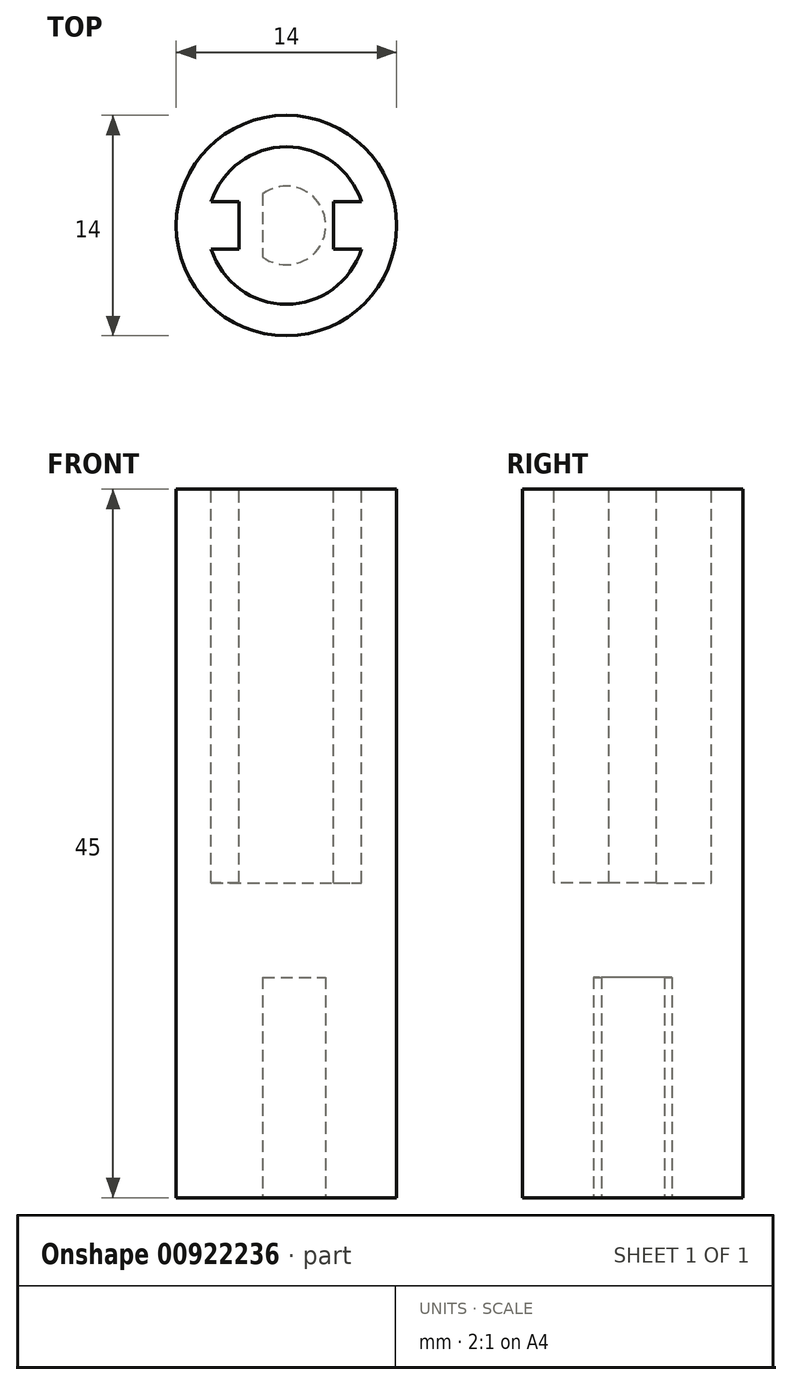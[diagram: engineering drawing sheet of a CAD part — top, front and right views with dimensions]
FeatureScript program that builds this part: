
annotation { "Feature Type Name" : "Feature", "Feature Type Description" : "" }
export const myFeature = defineFeature(function(context is Context, id is Id, definition is map)
    precondition{}
    {
        {
            var Q0;
            Q0=qCreatedBy(makeId("Top.planeOp"),FACE);
            var sketch = newSketch(context, id + "F0", { "sketchPlane" : qUnion([Q0])});
            skCircle(sketch, "E0", {"center": v(0, 0) * mm, "radius": 7 * mm});
            skSolve(sketch);
        }
        {
            var Q0;
            Q0=qSketchRegion(id+"F0",true);
            extrude(context, id + "F1", {"entities" : qUnion([Q0]), "depth" : 45 * mm, "offsetDistance" : 25 * mm});
        }
        {
            var Q0;
            Q0=makeQuery(id+"F1.opExtrude","CAP_FACE",FACE,{"disambiguationData":[OSD([sQuery(id+"F0.wireOp",EDGE,"E0")])],"isStart":false});
            var sketch = newSketch(context, id + "F2", { "sketchPlane" : qUnion([Q0])});
            skLineSegment(sketch, "E1", {"start": v(-12.72, 0) * mm, "end": v(15, 0) * mm, "construction": true});
            skLineSegment(sketch, "E2", {"start": v(0, 9.15) * mm, "end": v(0, -8.81) * mm, "construction": true});
            skLineSegment(sketch, "E3", {"start": v(-4.77, 1.5) * mm, "end": v(-3, 1.5) * mm});
            skLineSegment(sketch, "E4", {"start": v(-3, 1.5) * mm, "end": v(-3, -1.5) * mm});
            skLineSegment(sketch, "E5", {"start": v(-3, -1.5) * mm, "end": v(-4.77, -1.5) * mm});
            skLineSegment(sketch, "E6", {"start": v(4.77, 1.5) * mm, "end": v(3, 1.5) * mm});
            skLineSegment(sketch, "E7", {"start": v(3, 1.5) * mm, "end": v(3, -1.5) * mm});
            skLineSegment(sketch, "E8", {"start": v(3, -1.5) * mm, "end": v(4.77, -1.5) * mm});
            skArc(sketch, "E9", {"start": v(-4.77, -1.5) * mm, "mid": v(0, -5) * mm, "end": v(4.77, -1.5) * mm});
            skArc(sketch, "E10", {"start": v(4.77, 1.5) * mm, "mid": v(0, 5) * mm, "end": v(-4.77, 1.5) * mm});
            skSolve(sketch);
        }
        {
            var Q0;
            Q0=makeQuery(id+"F2.imprint","IMPRINT",FACE,{"disambiguationData":[TD([[makeQuery(id+"F2.imprint","IMPRINT",EDGE,{"derivedFrom":sQuery(id+"F2.wireOp",EDGE,"E3")}),1.0]])]});
            extrude(context, id + "F3", {"entities" : qUnion([Q0]), "operationType" : NewBodyOperationType.REMOVE, "oppositeDirection" : true, "depth" : 25 * mm, "offsetDistance" : 25 * mm});
        }
        {
            var Q0;
            Q0=makeQuery(id+"F1.opExtrude","CAP_FACE",FACE,{"disambiguationData":[OSD([sQuery(id+"F0.wireOp",EDGE,"E0")])],"isStart":true});
            var sketch = newSketch(context, id + "F4", { "sketchPlane" : qUnion([Q0])});
            skCircle(sketch, "E11", {"center": v(0, 0) * mm, "radius": 2.55 * mm});
            skSolve(sketch);
        }
        {
            var Q0;
            Q0=makeQuery(id+"F4.imprint","IMPRINT",FACE,{"disambiguationData":[TD([[makeQuery(id+"F4.imprint","IMPRINT",EDGE,{"derivedFrom":sQuery(id+"F4.wireOp",EDGE,"E11")}),1.0]])]});
            extrude(context, id + "F5", {"entities" : qUnion([Q0]), "operationType" : NewBodyOperationType.REMOVE, "oppositeDirection" : true, "depth" : 10 * mm, "offsetDistance" : 25 * mm});
        }
        {
            var Q0;
            Q0=makeQuery(id+"F5.boolean.opBoolean","COPY",FACE,{"derivedFrom":makeQuery(id+"F5.opExtrude","CAP_FACE",FACE,{"disambiguationData":[OSD([sQuery(id+"F4.wireOp",EDGE,"E11")])],"isStart":false})});
            var sketch = newSketch(context, id + "F6", { "sketchPlane" : qUnion([Q0])});
            skLineSegment(sketch, "E12", {"start": v(-1.5, -2) * mm, "end": v(-1.5, 2) * mm});
            skArc(sketch, "E13", {"start": v(-1.5, -2) * mm, "mid": v(2.5, 0) * mm, "end": v(-1.5, 2) * mm});
            skSolve(sketch);
        }
        {
            var Q0;
            Q0=makeQuery(id+"F6.imprint","IMPRINT",FACE,{"disambiguationData":[TD([[makeQuery(id+"F6.imprint","IMPRINT",EDGE,{"derivedFrom":sQuery(id+"F6.wireOp",EDGE,"E12")}),-1.0]])]});
            extrude(context, id + "F7", {"entities" : qUnion([Q0]), "operationType" : NewBodyOperationType.REMOVE, "oppositeDirection" : true, "depth" : 4 * mm, "offsetDistance" : 25 * mm});
        }
        {
            var Q0;
            Q0=makeQuery(id+"F5.boolean.opBoolean","COPY",FACE,{"derivedFrom":makeQuery(id+"F5.opExtrude","CAP_FACE",FACE,{"disambiguationData":[OSD([sQuery(id+"F4.wireOp",EDGE,"E11")])],"isStart":false})});
            extrude(context, id + "F8", {"entities" : qUnion([Q0]), "operationType" : NewBodyOperationType.ADD, "depth" : 10 * mm, "offsetDistance" : 25 * mm});
        }
    });
